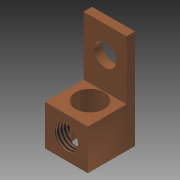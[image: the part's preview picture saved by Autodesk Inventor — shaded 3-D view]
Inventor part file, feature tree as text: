
AUTODESK INVENTOR PART (.ipt)
format: ipt  version: 2014 (Build 180170000, 170)  size: 134,144 bytes
history: native  units: mm (DEFAULTED — no unit token found)
features: sketch x4, extrude x2, hole x2
ambient origin geometry x8: Origin, YZ Plane, XZ Plane, XY Plane, X Axis, Y Axis, Z Axis, Center Point
bodies: Solid1 (feature_tree)
feature tree (8):
  extrude  "Extrusion1"  Depth=14.0mm
  extrude  "Extrusion2"  Depth=7.0mm
  hole  "Hole1"  [1 undecoded]
  hole  "Hole2"  [1 undecoded]
  sketch  "Sketch1"  dims[d0=12.75mm d1=14.0mm]
  sketch  "Sketch2"  dims[d2=6.375mm d3=7.0mm]
  sketch  "Sketch3"  dims[d4=12.0mm d5=0.0mm d7=2.5mm]
  sketch  "Sketch4"  dims[d8=17.5mm d9=0.0mm d10=8.0mm d11=6.375mm d12=6.5mm d13=6.0mm d14=4.0mm d15=2.0mm d16=14.3117mm d17=8.0mm d18=20.594885mm d19=6.375mm d20=6.0mm d21=6.917mm d22=6.0mm d23=4.0mm d24=2.0mm d25=14.3117mm d26=7.0mm d27=20.594885mm]
note: 2 required parameter values undecoded (feature->parameter linkage not recoverable at this tier; creation-order binding heuristic only, values carry confidence <= 0.55)
